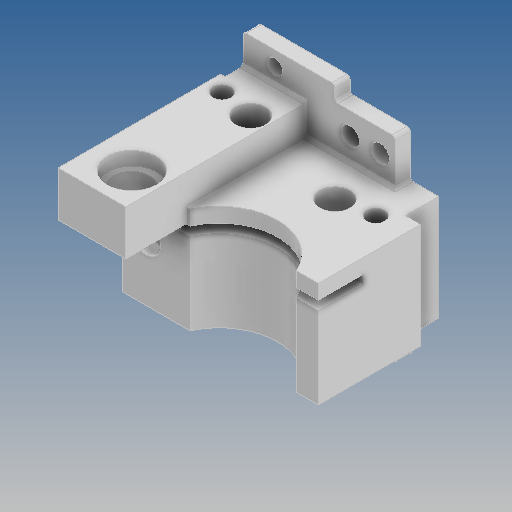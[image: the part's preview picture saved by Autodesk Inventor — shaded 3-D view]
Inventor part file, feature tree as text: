
AUTODESK INVENTOR PART (.ipt)
format: ipt  version: 2020 (Build 240168000, 168)  size: 374,272 bytes
history: native  units: mm
features: sketch x14, extrude x9, reference x8, hole x5, other x4, direct_edit x1, chamfer x1, fillet x1, move_body x1
ambient origin geometry x8: Origin, YZ Plane, XZ Plane, XY Plane, X Axis, Y Axis, Z Axis, Center Point
bodies: Solid1 (feature_tree)
feature tree (44):
  extrude  "Extrusion1"  Depth=35.0mm
  extrude  "Extrusion3"  Depth=2.9mm
  extrude  "Extrusion4"  Depth=15.0mm TaperAngle=0.0deg
  extrude  "Extrusion5"  TaperAngle=0.0deg  [1 undecoded]
  extrude  "Extrusion6"  Depth=8.0mm
  direct_edit  "Direct Edit1"
  hole  "Hole1"  [1 undecoded]
  hole  "Hole2"  [1 undecoded]
  hole  "Hole3"  [1 undecoded]
  extrude  "Extrusion7"  Depth=10.0mm
  hole  "Hole4"  [1 undecoded]
  hole  "Hole5"  [1 undecoded]
  extrude  "Extrusion8"  Depth=15.0mm
  extrude  "Extrusion9"  Depth=10.0mm
  chamfer  "Chamfer1"  Distance=5.0mm
  extrude  "Extrusion10"  Depth=5.0mm
  fillet  "Fillet1"  Radius=6.0mm
  sketch  "Sketch1"  dims[d0=65.0mm d1=35.0mm]
  sketch  "Sketch3"  dims[d2=45.0mm d3=0.0mm d8=2.9mm]
  sketch  "Sketch4"  dims[d9=5.0mm d10=15.0mm d11=0.0mm]
  sketch  "Sketch6"  dims[d12=38.8mm d14=0.0mm d15=0.0mm]
  sketch  "Sketch7"  dims[d16=8.0mm d17=25.0mm]
  sketch  "Sketch9"  dims[d18=5.0mm d19=11.0mm]
  reference  "Reference2"
  sketch  "Sketch10"  dims[d20=0.0mm d21=0.0mm d22=21.0mm]
  reference  "Reference3"
  reference  "Reference4"
  sketch  "Sketch11"  dims[d24=20.0mm d25=10.0mm d26=0.0mm]
  reference  "Reference5"
  reference  "Reference6"
  sketch  "Sketch13"  dims[d28=0.0mm d29=0.0mm d30=5.0mm]
  sketch  "Sketch14"  dims[d31=12.0mm d32=6.0mm d33=16.3mm d34=4.5mm d35=90.0deg d36=8.0mm d37=20.594885mm]
  sketch  "Sketch15"  dims[d38=10.0mm d39=6.0mm d40=16.3mm d41=4.5mm d42=90.0deg d43=8.0mm d44=20.594885mm]
  sketch  "Sketch16"  dims[d45=6.0mm d46=6.0mm d47=16.3mm d48=4.5mm d49=90.0deg d50=8.0mm d51=20.594885mm d53=10.0mm]
  sketch  "Sketch18"  dims[d54=15.0mm d55=10.0mm]
  sketch  "Sketch19"  dims[d56=0.0mm d57=0.0mm d58=7.5mm d59=5.0mm d60=6.0mm d61=10.0mm d62=5.0mm d63=90.0deg d64=8.0mm d65=20.594885mm d66=10.0mm d67=6.0mm d68=10.0mm d69=5.0mm d70=90.0deg d71=20.5mm d72=20.594885mm d74=15.0mm d75=10.0mm d76=5.0mm d77=5.0mm d78=6.0mm d79=10.0mm d80=6.0mm d81=6.0mm d82=5.0mm d83=0.0mm d84=10.0mm d85=5.0mm d86=10.0mm d87=5.0mm d88=0.0mm d89=1.0mm d90=2.0mm d91=45.0deg d92=7.55mm d93=10.5mm d94=11.0mm d95=1.5mm d96=0.0mm d99=1.0mm]
  reference  "Reference7"
  reference  "Reference8"
  reference  "Reference9"
  move_body  "Move1"
  other  "30-00 Injectomat suplimentar.iam"
  other  "ISO 1224-1 (Metric) 10 - 8 x 16 x 7:1"
  other  "0008-30-1007 Bara 8:2"
  other  "0008-30-002 Corp_Injectomat1:1"
note: 6 required parameter values undecoded (feature->parameter linkage not recoverable at this tier; creation-order binding heuristic only, values carry confidence <= 0.55)
